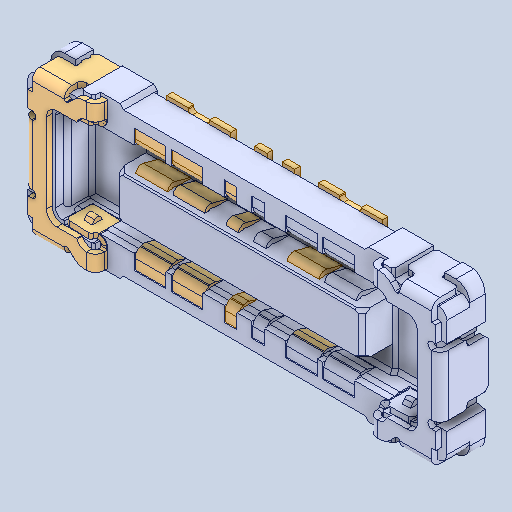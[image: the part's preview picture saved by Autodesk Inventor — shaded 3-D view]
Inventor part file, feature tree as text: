
AUTODESK INVENTOR PART (.ipt)
format: ipt  version: 2025 (Build 290162000, 162)  size: 940,032 bytes
history: native  units: mm
features: other x18, mirror x17
ambient origin geometry x8: Origin, YZ Plane, XZ Plane, XY Plane, X Axis, Y Axis, Z Axis, Center Point
bodies: Solid1 (feature_tree), Solid2 (feature_tree), Solid3 (feature_tree), Solid4 (feature_tree), Solid5 (feature_tree), Solid6 (feature_tree), Solid7 (feature_tree), Solid8 (feature_tree), Solid9 (feature_tree), Solid10 (feature_tree), Solid11 (feature_tree), Solid12 (feature_tree), Solid13 (feature_tree), Solid14 (feature_tree), Solid15 (feature_tree), Solid16 (feature_tree), Solid17 (feature_tree), Solid18 (feature_tree), Solid19 (feature_tree), Solid20 (feature_tree), Solid21 (feature_tree), Solid22 (feature_tree), Solid23 (feature_tree), Solid24 (feature_tree), Solid25 (feature_tree), Solid26 (feature_tree), Solid27 (feature_tree), Solid28 (feature_tree), Solid29 (feature_tree), Solid30 (feature_tree), Solid31 (feature_tree), Solid32 (feature_tree), Solid33 (feature_tree), Solid34 (feature_tree), Solid35 (feature_tree)
feature tree (35):
  mirror  "Mirror5[4]"
  mirror  "Mirror5[2]"
  other  "Boss-Extrude15"
  mirror  "Mirror5[5]"
  other  "Boss-Extrude11[4]"
  mirror  "Mirror5[6]"
  mirror  "Mirror5[3]"
  other  "Cut-Extrude9[2]"
  mirror  "Mirror5[9]"
  other  "Boss-Extrude14[1]"
  mirror  "Mirror5[10]"
  other  "Boss-Extrude12[1]"
  mirror  "Mirror5[7]"
  mirror  "Mirror5[11]"
  mirror  "Mirror4[4]"
  other  "Boss-Extrude13[2]"
  mirror  "Mirror5[1]"
  mirror  "Mirror2"
  other  "Boss-Extrude12[2]"
  mirror  "Mirror4[1]"
  other  "Boss-Extrude10[2]"
  other  "Boss-Extrude9[2]"
  other  "Boss-Extrude14[2]"
  other  "Boss-Extrude9[1]"
  other  "Cut-Extrude9[1]"
  other  "Boss-Extrude10[3]"
  other  "Boss-Extrude13[1]"
  other  "Boss-Extrude11[3]"
  other  "Cut-Extrude10"
  mirror  "Mirror5[12]"
  mirror  "Mirror4[2]"
  mirror  "Mirror4[3]"
  other  "LPattern1[1]"
  mirror  "Mirror5[8]"
  other  "LPattern1[3]"
